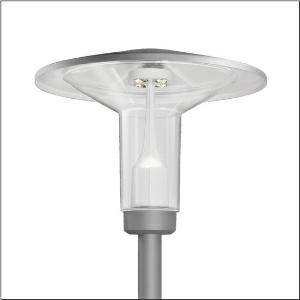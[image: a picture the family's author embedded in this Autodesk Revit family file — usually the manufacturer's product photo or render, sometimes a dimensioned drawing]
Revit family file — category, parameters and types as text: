
# Revit family: laterne_iq___p1_0a_5xa5255ff14h_2151
name_source: partatom
category: Lighting Fixtures
units: mm (PartAtom-declared; Revit-internal decimal feet)

## family parameters
Cut with Voids When Loaded = No
Host = Face
Light Source = No
Part Type = Normal
Room Calculation Point = No
Round Connector Dimension = Use Diameter
Shared = No

## types (1)
- --- (1 x LED, 1510 lm, 10.5 W, 3000K)
    Apparent Load = 11 VA
    CIE Flux Codes = 35 64 91 96 100
    Color Rendering = 70
    Color Temperature = 3000K
    Default Elevation = 1800 mm
    Description = Lantern iQ, mast luminaire, Module 540 iQ-SR, primary light control with 3 zone facetted reflector, of plastic, silver coated, highly specular, structured, primary optical cover: cover, of PMMA, transparent, light distribution: P1.0a, light emission: direct distribution, primary light characteristic: strongly asymmetric, installation type: post-top, LED, High Power LED, rated luminous flux: 1.510lm, luminous efficacy: 144lm/W, light colour: 730, colour temperature: 3000K, control gear: ECG iQ, control: Auto-Match, Temp-Guard, Lumen-Switch, Night-Set, Smart-Wire, Light-Fading, Desk-Remote (wireless, voltage-free reading and setting of iQ features in the workshop via application-optimized NFC function/RFID function), optimised constant luminous flux control (CLO 2.0), Street-Remote, presetting dimming logarithmic, with terminal, 6-pole, max. 2.5mm², mains connection: 230..240V, AC, 50/60Hz, start of lifetime: 11W, end of service life: 11W, reduction: 5W, luminaire housing, upper part, of glass-fibre reinforced polyester, coated, Siteco® metallic grey (DB 702S), diameter: 750mm, height: 583mm, spigot size: d x l = 76 x 70mm (post-top) | with reducer (optional accessory) 60 x 70mm, post-top mast mounting element, of diecast aluminium, coated, Siteco® metallic grey (DB 702S), Module 540 iQ-SR, traffic white (RAL 9016), equipment: standard, protection rating (complete): IP65, insulation class (complete): insulation class II (safety insulation), certification: CE, ENEC, VDE, packaging unit: 1 piece

Light Distribution: P1.0a
    Height = 583 mm
    Lamp = 1 x LED
    Lamp Light Flux = 1510 lm
    Lamp Power = 10.5 W
    Lamp count = 1
    Length = 750 mm
    Luminous efficacy = 144 lm/W
    Manufacturer = Siteco
    ModVariant = No
    Model = 5XA5255FF14H
    Number of Poles = 1
    OnlyDefault = Yes
    Power Factor = 1
    Product Name = Laterne iQ | P1.0a
    Product group = mast luminaire | pylon top
    ProductGroupID = 6100
    Protection Class = Protection class II
    Protection Degree = IP 65
    RLX_Detail_Level = 1
    RLX_Emergency_Light_Flux = 0 lm
    RLX_Emergency_Type = 0
    RLX_Emergency_Type_DB = No
    RlxData = <blob elided: 74049 chars, md5=1deea156>
    Socket = socket
    Standby Power = 0 W
    System Light Flux = 1510 lm
    System Power = 11 W
    Type Comments = factory setting: luminous flux: 100 % | dim-lin: 254 | 419 mA
    Type Image = l_1006050.jpg
    URL = http://relux.com
    VarID = @adj_092829
    Voltage = 0 V
    Weight = 0.00 kg
    Width = 0 mm  [stored 0 ft]

note: [stored X ft] marks values corroborated as IEEE doubles in the binary element streams (Revit-internal decimal feet)

## geometry (parser evidence)
native form markers: Blend x4, Sweep x11
no freeform markers — native parametric forms only
